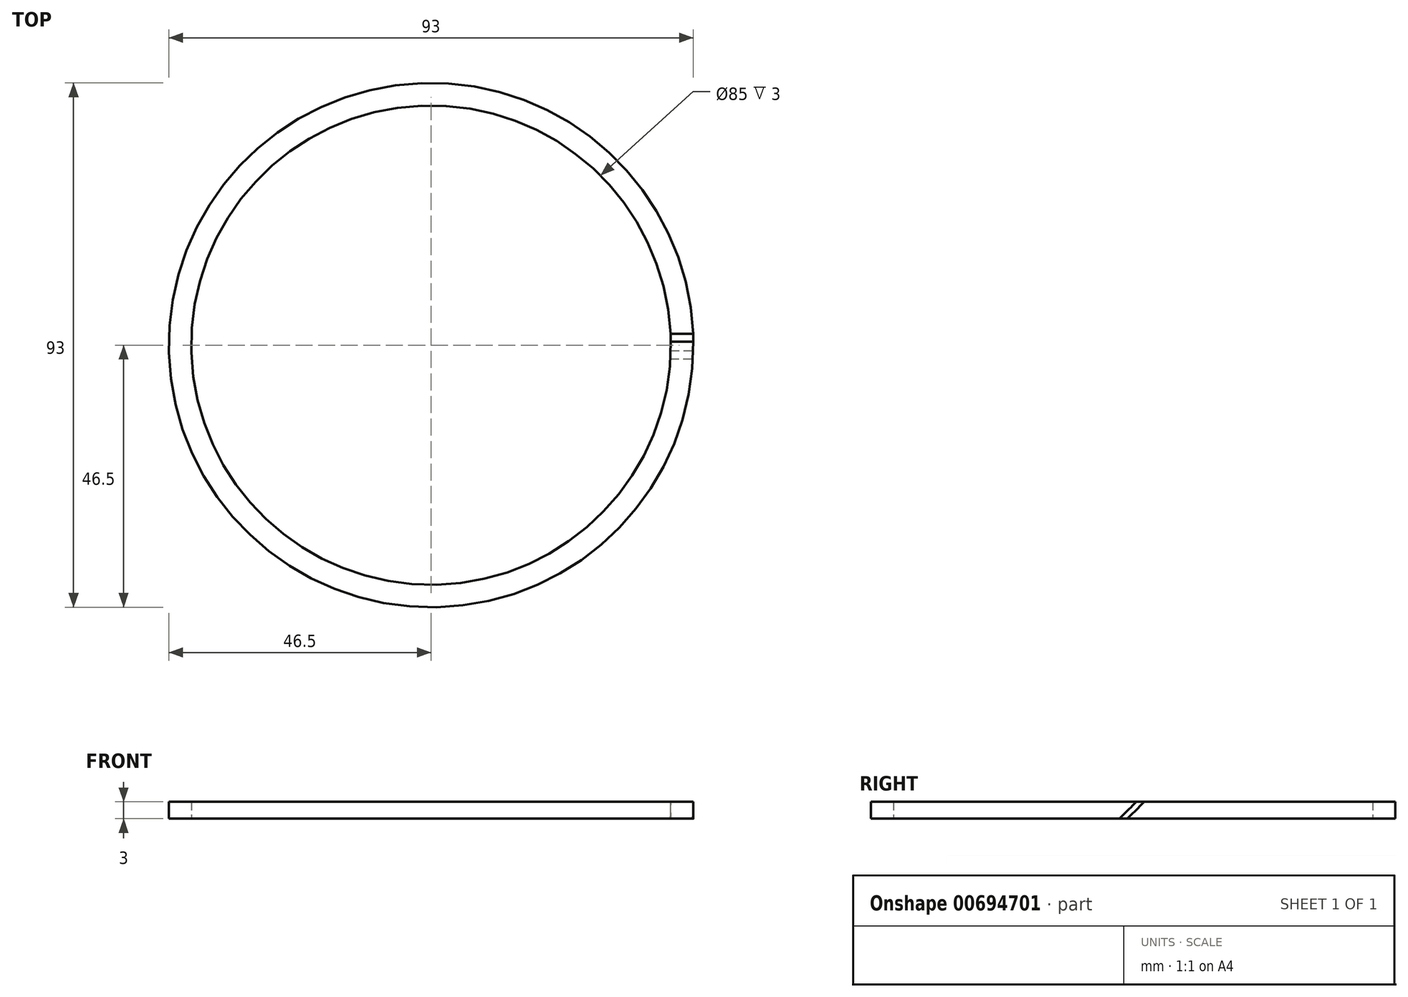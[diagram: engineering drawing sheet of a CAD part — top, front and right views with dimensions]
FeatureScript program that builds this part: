
annotation { "Feature Type Name" : "Feature", "Feature Type Description" : "" }
export const myFeature = defineFeature(function(context is Context, id is Id, definition is map)
    precondition{}
    {
        {
            var Q0;
            Q0=qCreatedBy(makeId("Top.planeOp"),FACE);
            var sketch = newSketch(context, id + "F0", { "sketchPlane" : qUnion([Q0])});
            skCircle(sketch, "E0", {"center": v(0, 0) * mm, "radius": 42.5 * mm});
            skCircle(sketch, "E1", {"center": v(0, 0) * mm, "radius": 46.5 * mm});
            skSolve(sketch);
        }
        {
            var Q0;
            Q0=makeQuery(id+"F0.imprint","IMPRINT",FACE,{"disambiguationData":[TD([[makeQuery(id+"F0.imprint","IMPRINT",EDGE,{"derivedFrom":sQuery(id+"F0.wireOp",EDGE,"E0")}),-1.0]])]});
            extrude(context, id + "F1", {"entities" : qUnion([Q0]), "depth" : 3 * mm, "offsetDistance" : 25 * mm});
        }
        {
            var Q0;
            Q0=qCreatedBy(makeId("Right.planeOp"),FACE);
            var sketch = newSketch(context, id + "F2", { "sketchPlane" : qUnion([Q0])});
            skLineSegment(sketch, "E2", {"start": v(-9.44, -8.42) * mm, "end": v(12.23, 13.24) * mm});
            skLineSegment(sketch, "E3.0", {"start": v(-11.83, -9.4) * mm, "end": v(9.84, 12.26) * mm});
            skLineSegment(sketch, "E4", {"start": v(9.84, 12.26) * mm, "end": v(12.23, 13.24) * mm});
            skLineSegment(sketch, "E5", {"start": v(-11.83, -9.4) * mm, "end": v(-9.44, -8.42) * mm});
            skSolve(sketch);
        }
        {
            var Q0;
            Q0 = qSketchRegion(id + "F2", true);
            extrude(context, id + "F3", {"entities" : qUnion([Q0]), "operationType" : NewBodyOperationType.REMOVE, "depth" : 91 * mm, "offsetDistance" : 25 * mm});
        }
    });
